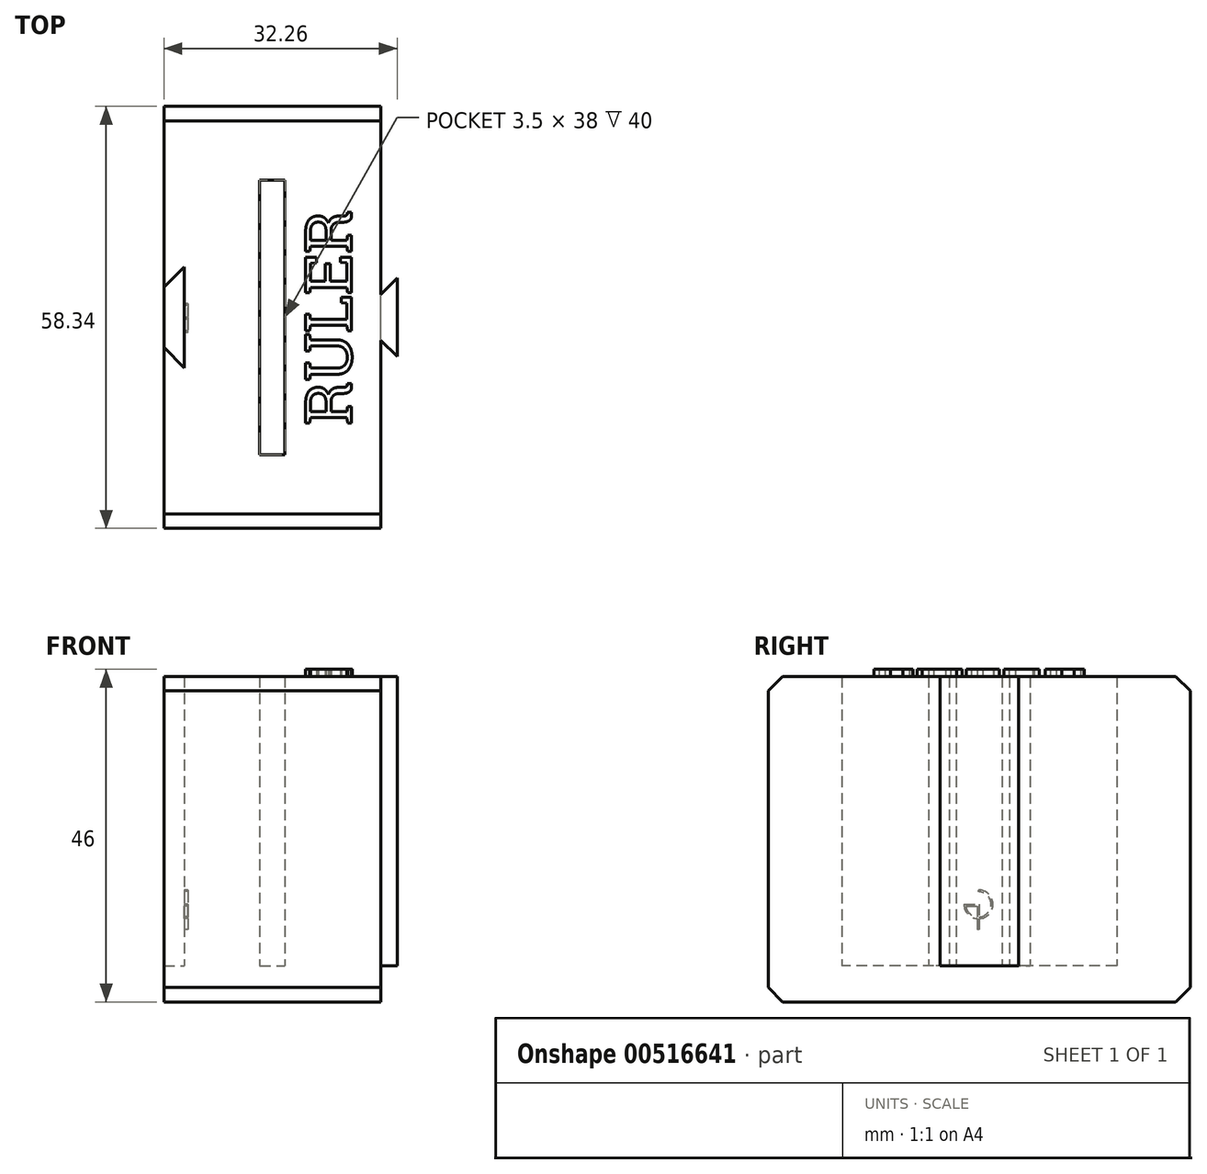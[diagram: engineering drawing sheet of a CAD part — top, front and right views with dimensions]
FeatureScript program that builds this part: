
annotation { "Feature Type Name" : "Feature", "Feature Type Description" : "" }
export const myFeature = defineFeature(function(context is Context, id is Id, definition is map)
    precondition{}
    {
        {
            var Q0;
            Q0=qCreatedBy(makeId("Top.planeOp"),FACE);
            var sketch = newSketch(context, id + "F0", { "sketchPlane" : qUnion([Q0])});
            skLineSegment(sketch, "E0", {"start": v(-15, 4.17) * mm, "end": v(-15, 29.17) * mm});
            skLineSegment(sketch, "E1", {"start": v(-15, 29.17) * mm, "end": v(15, 29.17) * mm});
            skLineSegment(sketch, "E2", {"start": v(15, 29.17) * mm, "end": v(15, 3.17) * mm});
            skLineSegment(sketch, "E3", {"start": v(-15, 4.17) * mm, "end": v(-12.17, 7) * mm});
            skLineSegment(sketch, "E4", {"start": v(-12.17, 7) * mm, "end": v(-12.17, 0) * mm});
            skLineSegment(sketch, "E5", {"start": v(15, 3.17) * mm, "end": v(17.26, 5.43) * mm});
            skLineSegment(sketch, "E6", {"start": v(17.26, 5.43) * mm, "end": v(17.26, -0.57) * mm});
            skLineSegment(sketch, "E7.MirrorCS", {"start": v(-15, -4.17) * mm, "end": v(-12.17, -7) * mm});
            skLineSegment(sketch, "E8.MirrorCS", {"start": v(15, -29.17) * mm, "end": v(15, -3.17) * mm});
            skLineSegment(sketch, "E9.MirrorCS", {"start": v(-12.17, -7) * mm, "end": v(-12.17, 0) * mm});
            skLineSegment(sketch, "E10.MirrorCS", {"start": v(-15, -4.17) * mm, "end": v(-15, -29.17) * mm});
            skLineSegment(sketch, "E11.MirrorCS", {"start": v(17.26, -5.43) * mm, "end": v(17.26, 0.57) * mm});
            skLineSegment(sketch, "E12.MirrorCS", {"start": v(15, -3.17) * mm, "end": v(17.26, -5.43) * mm});
            skLineSegment(sketch, "E13.MirrorCS", {"start": v(-15, -29.17) * mm, "end": v(15, -29.17) * mm});
            skLineSegment(sketch, "E14.bottom", {"start": v(-1.75, 19) * mm, "end": v(1.75, 19) * mm});
            skLineSegment(sketch, "E14.top", {"start": v(-1.75, -19) * mm, "end": v(1.75, -19) * mm});
            skLineSegment(sketch, "E14.left", {"start": v(-1.75, 19) * mm, "end": v(-1.75, -19) * mm});
            skLineSegment(sketch, "E14.right", {"start": v(1.75, 19) * mm, "end": v(1.75, -19) * mm});
            skPoint(sketch, "E14.middle", {"position": v(0, 0) * mm});
            skLineSegment(sketch, "E15", {"start": v(-15, 4.17) * mm, "end": v(-15, -4.17) * mm});
            skLineSegment(sketch, "E16", {"start": v(15, -3.17) * mm, "end": v(15, 3.17) * mm});
            skSolve(sketch);
        }
        {
            var Q0;
            Q0=makeQuery(id+"F0.imprint","IMPRINT",FACE,{"disambiguationData":[TD([[makeQuery(id+"F0.imprint","IMPRINT",EDGE,{"derivedFrom":sQuery(id+"F0.wireOp",EDGE,"E5")}),-1.0]])]});
            var Q1;
            Q1=makeQuery(id+"F0.imprint","IMPRINT",FACE,{"disambiguationData":[TD([[makeQuery(id+"F0.imprint","IMPRINT",EDGE,{"derivedFrom":sQuery(id+"F0.wireOp",EDGE,"E0")}),-1.0]])]});
            extrude(context, id + "F1", {"entities" : qUnion([Q0, Q1]), "depth" : 40 * mm, "offsetDistance" : 25 * mm});
        }
        {
            var Q0;
            Q0=makeQuery(id+"F0.imprint","IMPRINT",FACE,{"disambiguationData":[TD([[makeQuery(id+"F0.imprint","IMPRINT",EDGE,{"derivedFrom":sQuery(id+"F0.wireOp",EDGE,"E0")}),-1.0]])]});
            var Q1;
            Q1=makeQuery(id+"F0.imprint","IMPRINT",FACE,{"disambiguationData":[TD([[makeQuery(id+"F0.imprint","IMPRINT",EDGE,{"derivedFrom":sQuery(id+"F0.wireOp",EDGE,"E14.bottom")}),-1.0]])]});
            var Q2;
            Q2=makeQuery(id+"F0.imprint","IMPRINT",FACE,{"disambiguationData":[TD([[makeQuery(id+"F0.imprint","IMPRINT",EDGE,{"derivedFrom":sQuery(id+"F0.wireOp",EDGE,"E3")}),-1.0]])]});
            extrude(context, id + "F2", {"entities" : qUnion([Q0, Q1, Q2]), "operationType" : NewBodyOperationType.ADD, "oppositeDirection" : true, "depth" : 5 * mm, "offsetDistance" : 25 * mm});
        }
        {
            var Q0;
            Q0=makeQuery(id+"F2.opExtrude","CAP_EDGE",EDGE,{"disambiguationData":[OSD([sQuery(id+"F0.wireOp",EDGE,"E13.MirrorCS")])],"isStart":false});
            var Q1;
            Q1=makeQuery(id+"F2.opExtrude","CAP_EDGE",EDGE,{"disambiguationData":[OSD([sQuery(id+"F0.wireOp",EDGE,"E1")])],"isStart":false});
            var Q2;
            Q2=makeQuery(id+"F1.opExtrude","CAP_EDGE",EDGE,{"disambiguationData":[OSD([sQuery(id+"F0.wireOp",EDGE,"E13.MirrorCS")])],"isStart":false});
            var Q3;
            Q3=makeQuery(id+"F1.opExtrude","CAP_EDGE",EDGE,{"disambiguationData":[OSD([sQuery(id+"F0.wireOp",EDGE,"E1")])],"isStart":false});
            chamfer(context, id + "F3", {"entities" : qUnion([Q0, Q1, Q2, Q3]), "width" : 2 * mm, "tangentPropagation" : true});
        }
        {
            var Q0;
            Q0=makeQuery(id+"F1.opExtrude","CAP_FACE",FACE,{"disambiguationData":[OSD([sQuery(id+"F0.wireOp",EDGE,"E0"),sQuery(id+"F0.wireOp",EDGE,"E1"),sQuery(id+"F0.wireOp",EDGE,"E2"),sQuery(id+"F0.wireOp",EDGE,"E3"),sQuery(id+"F0.wireOp",EDGE,"E4"),sQuery(id+"F0.wireOp",EDGE,"E5"),sQuery(id+"F0.wireOp",EDGE,"E6"),sQuery(id+"F0.wireOp",EDGE,"E7.MirrorCS"),sQuery(id+"F0.wireOp",EDGE,"E8.MirrorCS"),sQuery(id+"F0.wireOp",EDGE,"E9.MirrorCS"),sQuery(id+"F0.wireOp",EDGE,"E10.MirrorCS"),sQuery(id+"F0.wireOp",EDGE,"E11.MirrorCS"),sQuery(id+"F0.wireOp",EDGE,"E12.MirrorCS"),sQuery(id+"F0.wireOp",EDGE,"E13.MirrorCS"),sQuery(id+"F0.wireOp",EDGE,"E14.bottom"),sQuery(id+"F0.wireOp",EDGE,"E14.top"),sQuery(id+"F0.wireOp",EDGE,"E14.left"),sQuery(id+"F0.wireOp",EDGE,"E14.right")])],"isStart":false});
            var sketch = newSketch(context, id + "F4", { "sketchPlane" : qUnion([Q0])});
            skText(sketch, "E17", { "text": "RULER", "fontName": "RobotoSlab-Regular.ttf"});
            const initialGuessF4  = {"E17": [0.01094, -0.0149, 0, 1, 0.00643]};
            skSetInitialGuess(sketch, initialGuessF4);
            skSolve(sketch);
        }
        {
            var Q0;
            Q0=qSketchRegion(id+"F4",true);
            extrude(context, id + "F5", {"entities" : qUnion([Q0]), "operationType" : NewBodyOperationType.ADD, "depth" : 1 * mm});
        }
        {
            var Q0;
            Q0=makeQuery(id+"F1.opExtrude","SWEPT_FACE",FACE,{"disambiguationData":[OSD([sQuery(id+"F0.wireOp",EDGE,"E4"),sQuery(id+"F0.wireOp",EDGE,"E9.MirrorCS")])]});
            var sketch = newSketch(context, id + "F6", { "sketchPlane" : qUnion([Q0])});
            skLineSegment(sketch, "E18.bottom", {"start": v(0.12, 10.5) * mm, "end": v(2.12, 10.5) * mm, "construction": true});
            skLineSegment(sketch, "E18.top", {"start": v(0.12, 8.5) * mm, "end": v(2.12, 8.5) * mm, "construction": true});
            skLineSegment(sketch, "E18.left", {"start": v(0.12, 10.5) * mm, "end": v(0.12, 8.5) * mm, "construction": true});
            skLineSegment(sketch, "E18.right", {"start": v(2.12, 10.5) * mm, "end": v(2.12, 8.5) * mm, "construction": true});
            skArc(sketch, "E19", {"start": v(0.12, 10.5) * mm, "mid": v(-1.3, 7.09) * mm, "end": v(2.12, 8.5) * mm});
            skLineSegment(sketch, "E20", {"start": v(0.12, 10.5) * mm, "end": v(0.12, 10.25) * mm});
            skLineSegment(sketch, "E21", {"start": v(2.12, 8.5) * mm, "end": v(1.87, 8.5) * mm});
            skArc(sketch, "E22", {"start": v(0.12, 10.25) * mm, "mid": v(-1.12, 7.26) * mm, "end": v(1.87, 8.5) * mm});
            skLineSegment(sketch, "E23", {"start": v(1.87, 8.5) * mm, "end": v(0, 8.5) * mm});
            skLineSegment(sketch, "E24", {"start": v(0, 8.5) * mm, "end": v(0, 5) * mm});
            skLineSegment(sketch, "E25", {"start": v(0, 5) * mm, "end": v(0.25, 5) * mm});
            skLineSegment(sketch, "E26", {"start": v(1.85, 8.25) * mm, "end": v(0.25, 8.25) * mm});
            skLineSegment(sketch, "E27", {"start": v(0.25, 8.25) * mm, "end": v(0.25, 5) * mm});
            skSolve(sketch);
        }
        {
            var Q0;
            {var subQ0=sQuery(id+"F6.wireOp",EDGE,"E20");Q0=makeQuery(id+"F6.imprint","IMPRINT",FACE,{"disambiguationData":[TD([[makeQuery(id+"F6.imprint","IMPRINT",EDGE,{"derivedFrom":subQ0}),-1.0]])]});}
            var Q1;
            {var subQ1=sQuery(id+"F6.wireOp",EDGE,"E23");Q1=makeQuery(id+"F6.imprint","IMPRINT",FACE,{"disambiguationData":[TD([[makeQuery(id+"F6.imprint","IMPRINT",EDGE,{"derivedFrom":subQ1}),1.0]])]});}
            var Q2;
            {var subQ1=sQuery(id+"F6.wireOp",EDGE,"E21");Q2=makeQuery(id+"F6.imprint","IMPRINT",FACE,{"disambiguationData":[TD([[makeQuery(id+"F6.imprint","IMPRINT",EDGE,{"derivedFrom":subQ1}),1.0]])]});}
            var Q3;
            {var subQ0=sQuery(id+"F6.wireOp",EDGE,"E24");var subQ1=sQuery(id+"F6.wireOp",EDGE,"E19");var subQ2=makeQuery(id+"F6.imprint","INTERSECT",VERTEX,{"derivedFrom":[subQ1,subQ0]});Q3=makeQuery(id+"F6.imprint","IMPRINT",FACE,{"disambiguationData":[TD([[makeQuery(id+"F6.imprint","IMPRINT",EDGE,{"disambiguationData":[TD([[subQ2,-1.0]])],"derivedFrom":subQ1}),1.0]])]});}
            var Q4;
            {var subQ5=sQuery(id+"F6.wireOp",EDGE,"E25");Q4=makeQuery(id+"F6.imprint","IMPRINT",FACE,{"disambiguationData":[TD([[makeQuery(id+"F6.imprint","IMPRINT",EDGE,{"derivedFrom":subQ5}),1.0]])]});}
            extrude(context, id + "F7", {"entities" : qUnion([Q0, Q1, Q2, Q3, Q4]), "operationType" : NewBodyOperationType.REMOVE, "oppositeDirection" : true, "depth" : .5 * mm, "offsetDistance" : 25 * mm});
        }
    });
